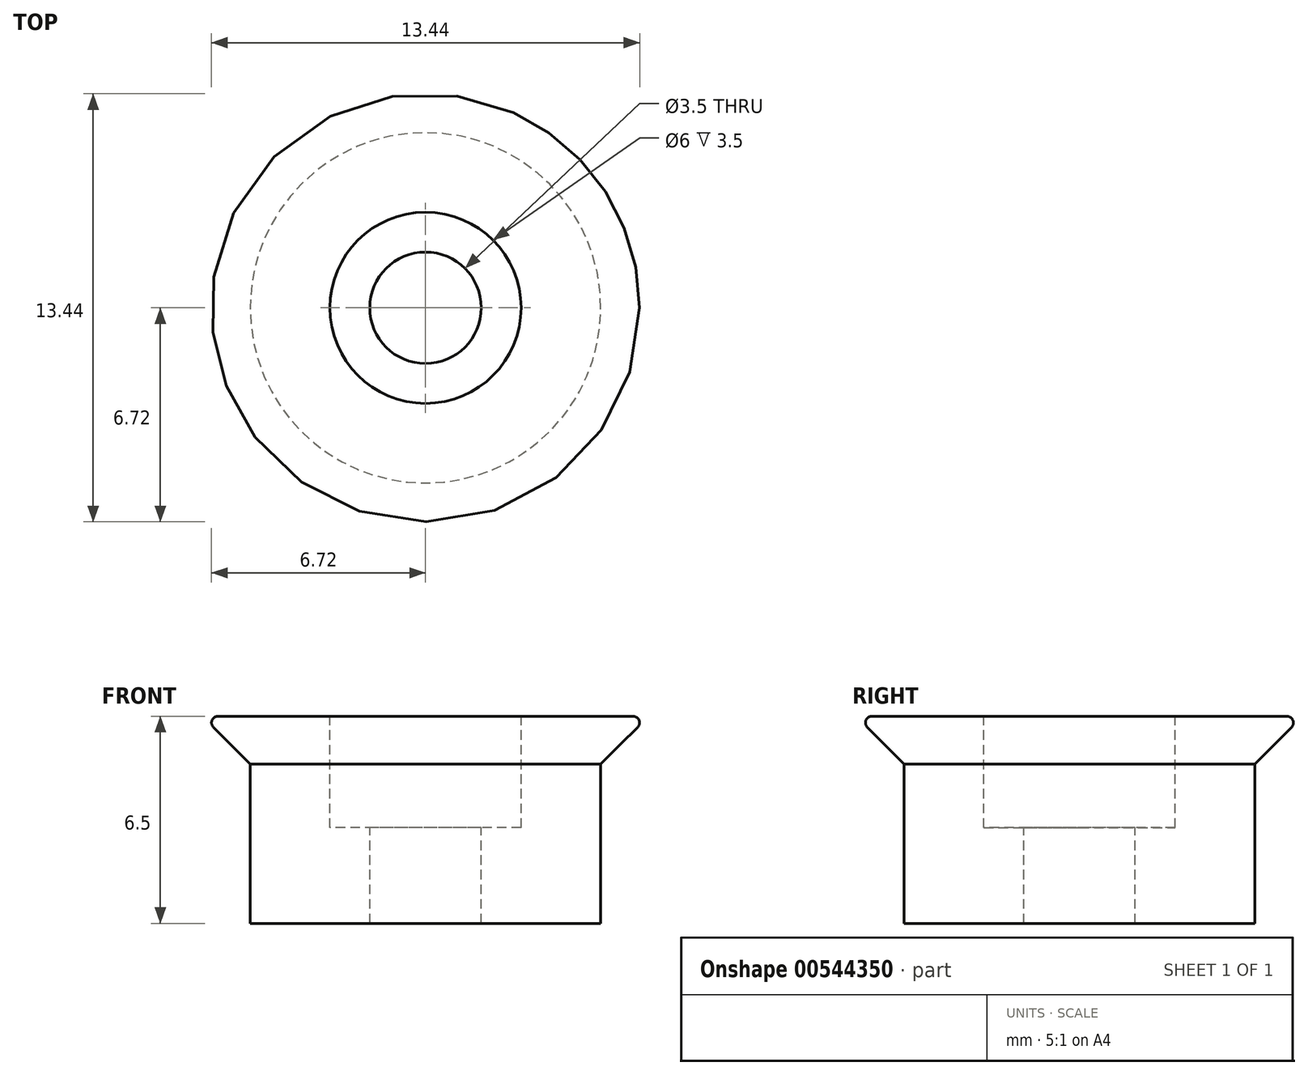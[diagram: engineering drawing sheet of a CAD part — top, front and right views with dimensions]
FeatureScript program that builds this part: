
annotation { "Feature Type Name" : "Feature", "Feature Type Description" : "" }
export const myFeature = defineFeature(function(context is Context, id is Id, definition is map)
    precondition{}
    {
        {
            var Q0;
            Q0=qCreatedBy(makeId("Top.planeOp"),FACE);
            var sketch = newSketch(context, id + "F0", { "sketchPlane" : qUnion([Q0])});
            skCircle(sketch, "E0", {"center": v(0, 0) * mm, "radius": 5.5 * mm});
            skSolve(sketch);
        }
        {
            var Q0;
            Q0 = qSketchRegion(id + "F0", true);
            extrude(context, id + "F1", {"entities" : qUnion([Q0]), "depth" : 5 * mm, "offsetDistance" : 25 * mm});
        }
        {
            var Q0;
            Q0=makeQuery(id+"F1.opExtrude","CAP_FACE",FACE,{"disambiguationData":[OSD([sQuery(id+"F0.wireOp",EDGE,"E0")])],"isStart":false});
            extrude(context, id + "F2", {"entities" : qUnion([Q0]), "operationType" : NewBodyOperationType.ADD, "depth" : 1.5 * mm, "offsetDistance" : 25 * mm, "hasDraft" : true, "draftAngle" : 45 * degree});
        }
        {
            var Q0;
            Q0=makeQuery(id+"F2.opExtrude","CAP_EDGE",EDGE,{"disambiguationData":[OSD([sQuery(id+"F0.wireOp",EDGE,"E0")])],"isStart":false});
            fillet(context, id + "F3", {"entities" : qUnion([Q0]), "radius" : 0.2 * mm, "tangentPropagation" : true, "allowEdgeOverflow" : false});
        }
        {
            var Q0;
            Q0=makeQuery(id+"F2.opExtrude","CAP_FACE",FACE,{"disambiguationData":[OSD([sQuery(id+"F0.wireOp",EDGE,"E0")])],"isStart":false});
            var sketch = newSketch(context, id + "F4", { "sketchPlane" : qUnion([Q0])});
            skCircle(sketch, "E1", {"center": v(0, 0) * mm, "radius": 3 * mm});
            skCircle(sketch, "E2", {"center": v(0, 0) * mm, "radius": 1.75 * mm});
            skSolve(sketch);
        }
        {
            var Q0;
            Q0=makeQuery(id+"F4.imprint","IMPRINT",FACE,{"disambiguationData":[TD([[makeQuery(id+"F4.imprint","IMPRINT",EDGE,{"derivedFrom":sQuery(id+"F4.wireOp",EDGE,"E2")}),1.0]])]});
            extrude(context, id + "F5", {"entities" : qUnion([Q0]), "operationType" : NewBodyOperationType.REMOVE, "endBound" : BoundingType.THROUGH_ALL, "oppositeDirection" : true, "depth" : 25 * mm, "offsetDistance" : 25 * mm});
        }
        {
            var Q0;
            Q0=makeQuery(id+"F4.imprint","IMPRINT",FACE,{"disambiguationData":[TD([[makeQuery(id+"F4.imprint","IMPRINT",EDGE,{"derivedFrom":sQuery(id+"F4.wireOp",EDGE,"E1")}),1.0]])]});
            extrude(context, id + "F6", {"entities" : qUnion([Q0]), "operationType" : NewBodyOperationType.REMOVE, "oppositeDirection" : true, "depth" : 3.5 * mm, "offsetDistance" : 25 * mm});
        }
    });
